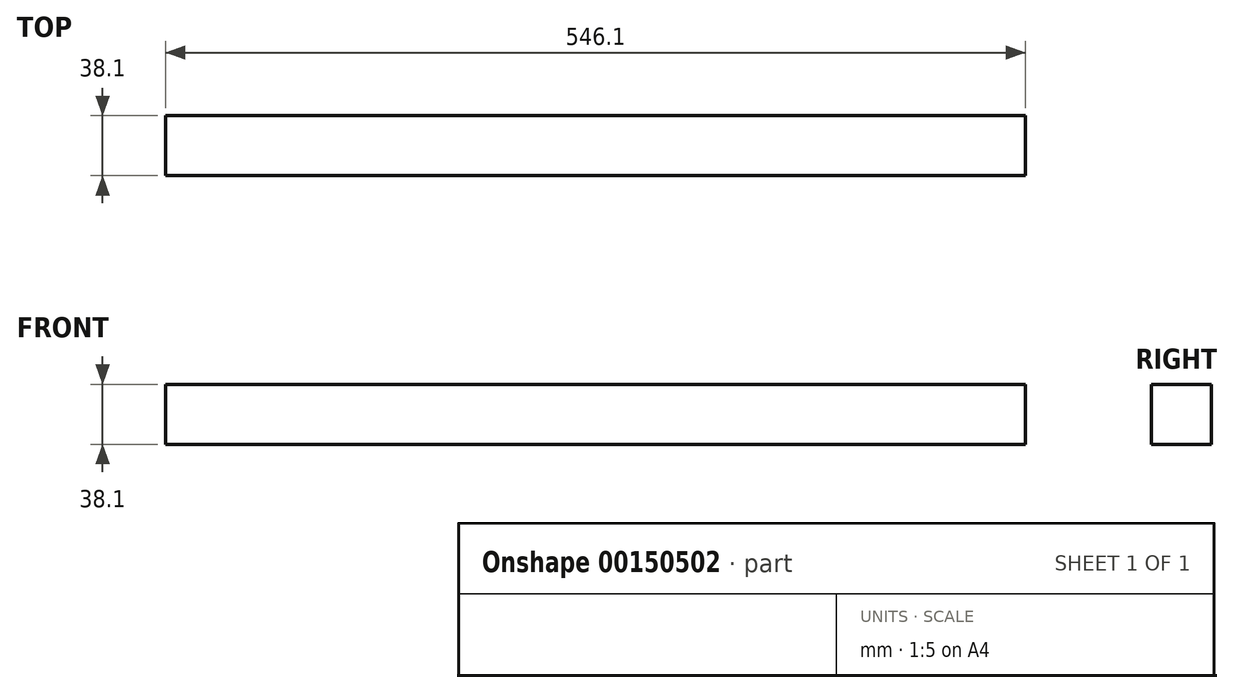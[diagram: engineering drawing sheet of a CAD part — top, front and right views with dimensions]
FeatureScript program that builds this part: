
annotation { "Feature Type Name" : "Feature", "Feature Type Description" : "" }
export const myFeature = defineFeature(function(context is Context, id is Id, definition is map)
    precondition{}
    {
        {
            var Q0;
            Q0=qCreatedBy(makeId("Front.planeOp"),FACE);
            var sketch = newSketch(context, id + "F0", { "sketchPlane" : qUnion([Q0])});
            skLineSegment(sketch, "E0.bottom", {"start": v(273.05, 19.05) * mm, "end": v(-273.05, 19.05) * mm});
            skLineSegment(sketch, "E0.top", {"start": v(273.05, -19.05) * mm, "end": v(-273.05, -19.05) * mm});
            skLineSegment(sketch, "E0.left", {"start": v(273.05, 19.05) * mm, "end": v(273.05, -19.05) * mm});
            skLineSegment(sketch, "E0.right", {"start": v(-273.05, 19.05) * mm, "end": v(-273.05, -19.05) * mm});
            skPoint(sketch, "E0.middle", {"position": v(0, 0) * mm});
            skSolve(sketch);
        }
        {
            var Q0;
            Q0=qSketchRegion(id+"F0",true);
            extrude(context, id + "F1", {"entities" : qUnion([Q0]), "depth" : 38.1 * mm});
        }
    });
